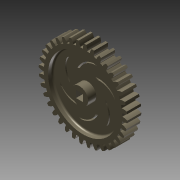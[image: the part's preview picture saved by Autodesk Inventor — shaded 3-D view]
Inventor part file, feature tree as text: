
AUTODESK INVENTOR PART (.ipt)
format: ipt  version: 2013 (Build 170138000, 138)  size: 1,138,176 bytes
history: native  units: mm (DEFAULTED — no unit token found)
features: imported_body x1, sketch x1, other x1, extrude x1
ambient origin geometry x8: Origin, YZ Plane, XZ Plane, XY Plane, X Axis, Y Axis, Z Axis, Center Point
bodies: Solid1 (feature_tree)
feature tree (4):
  imported_body  "Base1"
  sketch  "Sketch1"  dims[d0=25.4mm d1=0.0mm d2=0.0mm d3=0.0mm]
  other  "Srf1"
  extrude  "ExtrusionSrf1"  TaperAngle=0.0deg  [1 undecoded]
note: 1 required parameter value undecoded (feature->parameter linkage not recoverable at this tier; creation-order binding heuristic only, values carry confidence <= 0.55)
